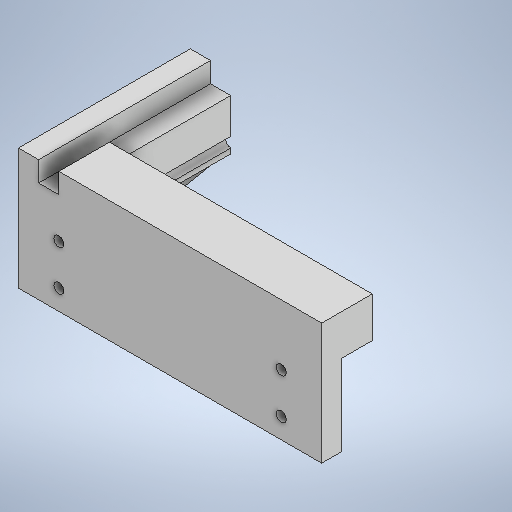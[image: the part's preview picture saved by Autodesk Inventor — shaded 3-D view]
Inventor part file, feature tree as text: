
AUTODESK INVENTOR PART (.ipt)
format: ipt  version: 2025.3 (Build 293356000, 356)  size: 563,200 bytes
history: native  units: mm
features: extrude x4, sketch x2, other x1, projected_geometry x1
ambient origin geometry x8: Origin, YZ Plane, XZ Plane, XY Plane, X Axis, Y Axis, Z Axis, Center Point
bodies: Body1 (feature_tree)
feature tree (8):
  other  "솔리드1"
  sketch  "스케치1"
  extrude  "돌출1"  Depth=5.0mm
  extrude  "돌출2"  Depth=30.0mm
  extrude  "돌출3"  Depth=20.0mm
  extrude  "돌출4"  Depth=20.0mm
  sketch  "스케치2"
  projected_geometry  "투영된 루프1"
